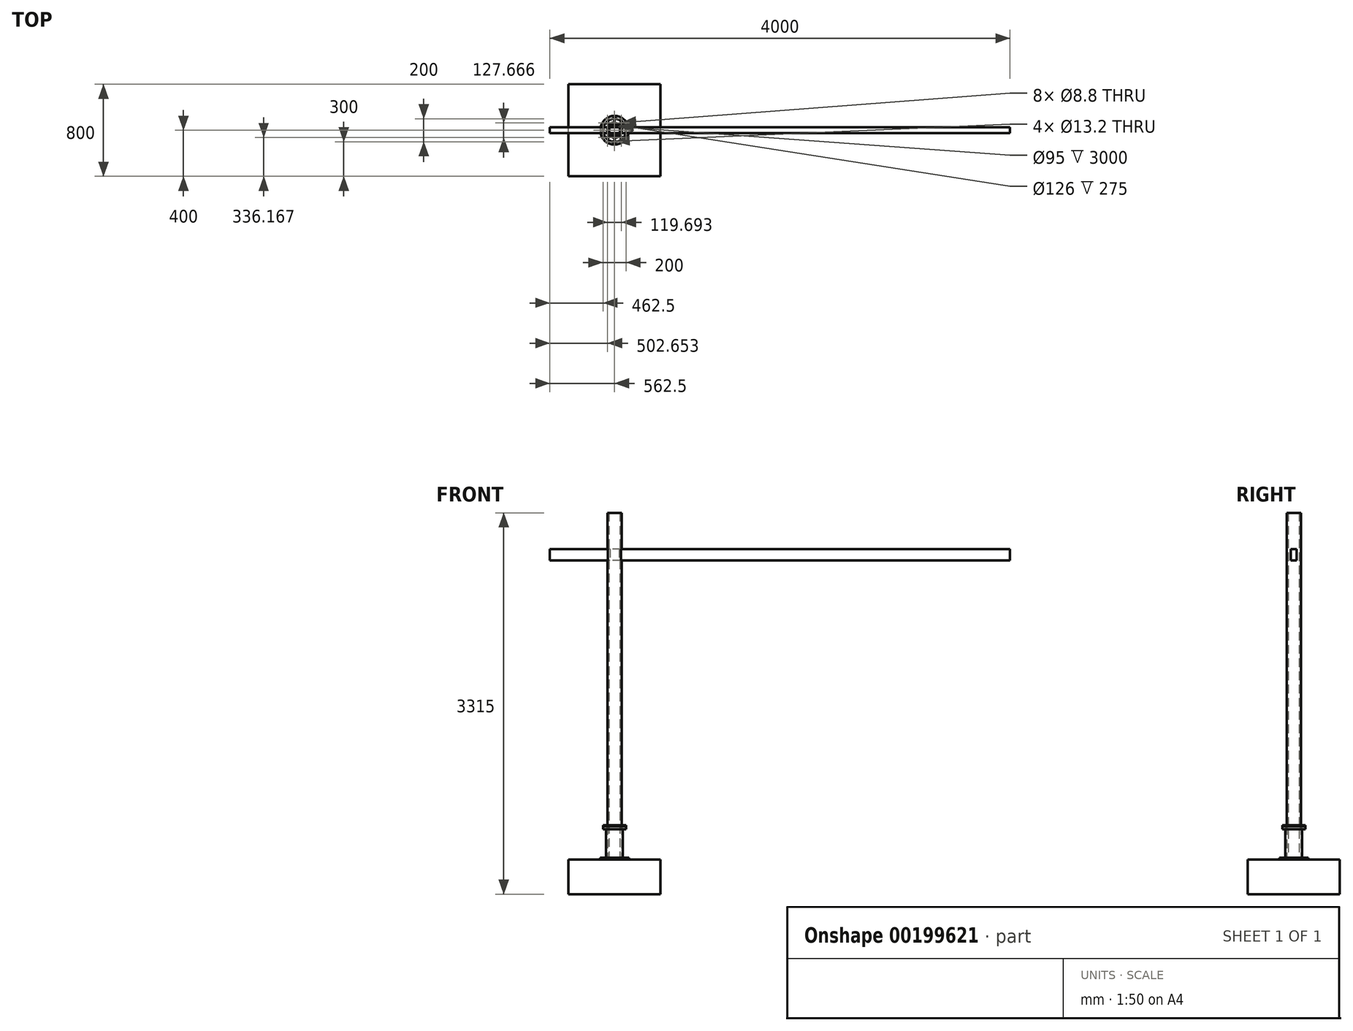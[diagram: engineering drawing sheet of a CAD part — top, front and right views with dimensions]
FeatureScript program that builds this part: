
annotation { "Feature Type Name" : "Feature", "Feature Type Description" : "" }
export const myFeature = defineFeature(function(context is Context, id is Id, definition is map)
    precondition{}
    {
        {
            var Q0;
            Q0=qCreatedBy(makeId("Top.planeOp"),FACE);
            var sketch = newSketch(context, id + "F0", { "sketchPlane" : qUnion([Q0])});
            skLineSegment(sketch, "E0.bottom", {"start": v(-400, -400) * mm, "end": v(400, -400) * mm});
            skLineSegment(sketch, "E0.top", {"start": v(-400, 400) * mm, "end": v(400, 400) * mm});
            skLineSegment(sketch, "E0.left", {"start": v(-400, -400) * mm, "end": v(-400, 400) * mm});
            skLineSegment(sketch, "E0.right", {"start": v(400, -400) * mm, "end": v(400, 400) * mm});
            skPoint(sketch, "E0.middle", {"position": v(0, 0) * mm});
            skSolve(sketch);
        }
        {
            var Q0;
            Q0 = qSketchRegion(id + "F0", true);
            extrude(context, id + "F1", {"entities" : qUnion([Q0]), "oppositeDirection" : true, "depth" : 300 * mm});
        }
        {
            var Q0;
            Q0=makeQuery(id+"F1.opExtrude","CAP_FACE",FACE,{"disambiguationData":[OSD([sQuery(id+"F0.wireOp",EDGE,"E0.bottom"),sQuery(id+"F0.wireOp",EDGE,"E0.top"),sQuery(id+"F0.wireOp",EDGE,"E0.left"),sQuery(id+"F0.wireOp",EDGE,"E0.right")])],"isStart":true});
            var sketch = newSketch(context, id + "F2", { "sketchPlane" : qUnion([Q0])});
            skCircle(sketch, "E1", {"center": v(0, 0) * mm, "radius": 125 * mm});
            skSolve(sketch);
        }
        {
            var Q0;
            Q0 = qSketchRegion(id + "F2", true);
            extrude(context, id + "F3", {"entities" : qUnion([Q0]), "depth" : 15 * mm});
        }
        {
            var Q0;
            Q0=makeQuery(id+"F3.opExtrude","CAP_FACE",FACE,{"disambiguationData":[OSD([sQuery(id+"F2.wireOp",EDGE,"E1")])],"isStart":false});
            var sketch = newSketch(context, id + "F4", { "sketchPlane" : qUnion([Q0])});
            skCircle(sketch, "E2", {"center": v(0, 0) * mm, "radius": 62.5 * mm});
            skCircle(sketch, "E3.0", {"center": v(0, 0) * mm, "radius": 47.5 * mm});
            skSolve(sketch);
        }
        {
            var Q0;
            Q0 = qSketchRegion(id + "F4", true);
            extrude(context, id + "F5", {"entities" : qUnion([Q0]), "depth" : 3000 * mm});
        }
        {
            var Q0;
            Q0=qCreatedBy(makeId("Right.planeOp"),FACE);
            cPlane(context, id + "F6", {"entities" : qUnion([Q0]), "cplaneType" : CPlaneType.OFFSET, "offset" : 62.5 * mm, "oppositeDirection" : true, "width" : 150 * mm, "height" : 150 * mm});
        }
        {
            var Q0;
            Q0=qCreatedBy(id+"F6.planeOp",FACE);
            var sketch = newSketch(context, id + "F7", { "sketchPlane" : qUnion([Q0])});
            skLineSegment(sketch, "E4.bottom", {"start": v(-25, 2700) * mm, "end": v(25, 2700) * mm});
            skLineSegment(sketch, "E4.top", {"start": v(-25, 2600) * mm, "end": v(25, 2600) * mm});
            skLineSegment(sketch, "E4.left", {"start": v(-25, 2700) * mm, "end": v(-25, 2600) * mm});
            skLineSegment(sketch, "E4.right", {"start": v(25, 2700) * mm, "end": v(25, 2600) * mm});
            skPoint(sketch, "E4.middle", {"position": v(0, 2650) * mm});
            skSolve(sketch);
        }
        {
            var Q0;
            Q0 = qSketchRegion(id + "F7", true);
            extrude(context, id + "F8", {"entities" : qUnion([Q0]), "operationType" : NewBodyOperationType.REMOVE, "endBound" : BoundingType.THROUGH_ALL, "depth" : 25 * mm});
        }
        {
            var Q0;
            Q0=qCreatedBy(id+"F6.planeOp",FACE);
            var sketch = newSketch(context, id + "F9", { "sketchPlane" : qUnion([Q0])});
            skLineSegment(sketch, "E5.bottom", {"start": v(25, 2600) * mm, "end": v(-25, 2600) * mm});
            skLineSegment(sketch, "E5.top", {"start": v(25, 2700) * mm, "end": v(-25, 2700) * mm});
            skLineSegment(sketch, "E5.left", {"start": v(25, 2600) * mm, "end": v(25, 2700) * mm});
            skLineSegment(sketch, "E5.right", {"start": v(-25, 2600) * mm, "end": v(-25, 2700) * mm});
            skSolve(sketch);
        }
        {
            var Q0;
            Q0 = qSketchRegion(id + "F9", true);
            extrude(context, id + "F10", {"entities" : qUnion([Q0]), "depth" : 3500 * mm, "hasSecondDirection" : true, "secondDirectionOppositeDirection" : true, "secondDirectionDepth" : 500 * mm});
        }
        {
            var Q0;
            Q0=makeQuery(id+"F3.opExtrude","CAP_FACE",FACE,{"disambiguationData":[OSD([sQuery(id+"F2.wireOp",EDGE,"E1")])],"isStart":false});
            var sketch = newSketch(context, id + "F11", { "sketchPlane" : qUnion([Q0])});
            skCircle(sketch, "E6", {"center": v(0, 0) * mm, "radius": 73 * mm});
            skCircle(sketch, "E7", {"center": v(0, 0) * mm, "radius": 63 * mm});
            skSolve(sketch);
        }
        {
            var Q0;
            Q0 = qSketchRegion(id + "F11", true);
            extrude(context, id + "F12", {"entities" : qUnion([Q0]), "operationType" : NewBodyOperationType.ADD, "depth" : 250 * mm});
        }
        {
            var Q0;
            Q0=makeQuery(id+"F12.opExtrude","CAP_FACE",FACE,{"disambiguationData":[OSD([sQuery(id+"F11.wireOp",EDGE,"E6"),sQuery(id+"F11.wireOp",EDGE,"E7")])],"isStart":false});
            var sketch = newSketch(context, id + "F13", { "sketchPlane" : qUnion([Q0])});
            skCircle(sketch, "E8", {"center": v(0, 0) * mm, "radius": 63 * mm});
            skCircle(sketch, "E9", {"center": v(0, 0) * mm, "radius": 100 * mm});
            skSolve(sketch);
        }
        {
            var Q0;
            Q0 = qSketchRegion(id + "F13", true);
            extrude(context, id + "F14", {"entities" : qUnion([Q0]), "operationType" : NewBodyOperationType.ADD, "depth" : 25 * mm});
        }
        {
            var Q0;
            Q0=makeQuery(id+"F14.opExtrude","CAP_FACE",FACE,{"disambiguationData":[OSD([sQuery(id+"F13.wireOp",EDGE,"E8"),sQuery(id+"F13.wireOp",EDGE,"E9")])],"isStart":false});
            var sketch = newSketch(context, id + "F15", { "sketchPlane" : qUnion([Q0])});
            skCircle(sketch, "E10", {"center": v(0, 0) * mm, "radius": 63 * mm});
            skCircle(sketch, "E11", {"center": v(0, 0) * mm, "radius": 58 * mm});
            skSolve(sketch);
        }
        {
            var Q0;
            Q0 = qSketchRegion(id + "F15", true);
            extrude(context, id + "F16", {"entities" : qUnion([Q0]), "operationType" : NewBodyOperationType.REMOVE, "depth" : 10 * mm});
        }
        {
            var Q0;
            Q0=makeQuery(id+"F14.opExtrude","CAP_FACE",FACE,{"disambiguationData":[OSD([sQuery(id+"F13.wireOp",EDGE,"E8"),sQuery(id+"F13.wireOp",EDGE,"E9")])],"isStart":false});
            var sketch = newSketch(context, id + "F17", { "sketchPlane" : qUnion([Q0])});
            skArc(sketch, "E12", {"start": v(0, -59) * mm, "mid": v(59, 0) * mm, "end": v(0, 59) * mm});
            skArc(sketch, "E13", {"start": v(0, -100) * mm, "mid": v(100, 0) * mm, "end": v(0, 100) * mm});
            skLineSegment(sketch, "E14", {"start": v(0, 100) * mm, "end": v(0, 59) * mm});
            skLineSegment(sketch, "E15.trimOffspring", {"start": v(0, -59) * mm, "end": v(0, -100) * mm});
            skSolve(sketch);
        }
        {
            var Q0;
            Q0 = qSketchRegion(id + "F17", true);
            extrude(context, id + "F18", {"entities" : qUnion([Q0]), "depth" : 8 * mm});
        }
        {
            var Q0;
            Q0=makeQuery(id+"F18.opExtrude","SWEPT_BODY",BODY,{"disambiguationData":[OSD([sQuery(id+"F17.wireOp",EDGE,"E12"),sQuery(id+"F17.wireOp",EDGE,"E13"),sQuery(id+"F17.wireOp",EDGE,"E14"),sQuery(id+"F17.wireOp",EDGE,"E15.trimOffspring")])]});
            var Q1;
            Q1=makeQuery(id+"F18.opExtrude","SWEPT_FACE",FACE,{"disambiguationData":[OSD([sQuery(id+"F17.wireOp",EDGE,"E15.trimOffspring")])]});
            mirror(context, id + "F19", {"entities" : qUnion([Q0]), "mirrorPlane" : qUnion([Q1])});
        }
        {
            var Q0;
            Q0=makeQuery(id+"F18.opExtrude","CAP_FACE",FACE,{"disambiguationData":[OSD([sQuery(id+"F17.wireOp",EDGE,"E12"),sQuery(id+"F17.wireOp",EDGE,"E13"),sQuery(id+"F17.wireOp",EDGE,"E14"),sQuery(id+"F17.wireOp",EDGE,"E15.trimOffspring")])],"isStart":false});
            var sketch = newSketch(context, id + "F20", { "sketchPlane" : qUnion([Q0])});
            skLineSegment(sketch, "E16", {"start": v(-59.85, -63.83) * mm, "end": v(59.85, 63.83) * mm, "construction": true});
            skCircle(sketch, "E17", {"center": v(0, 0) * mm, "radius": 87.5 * mm, "construction": true});
            skLineSegment(sketch, "E18.MirrorCS", {"start": v(59.85, -63.83) * mm, "end": v(-59.85, 63.83) * mm, "construction": true});
            skSolve(sketch);
        }
        {
            var Q0;
            Q0=sQuery(id+"F20.wireOp",VERTEX,"E18.MirrorCS.end");
            var Q1;
            Q1=sQuery(id+"F20.wireOp",VERTEX,"E16.end");
            var Q2;
            Q2=sQuery(id+"F20.wireOp",VERTEX,"E18.MirrorCS.start");
            var Q3;
            Q3=sQuery(id+"F20.wireOp",VERTEX,"E16.start");
            var Q4;
            Q4=makeQuery(id+"F3.opExtrude","SWEPT_BODY",BODY,{"disambiguationData":[OSD([sQuery(id+"F2.wireOp",EDGE,"E1")])]});
            var Q5;
            Q5=makeQuery(id+"F18.opExtrude","SWEPT_BODY",BODY,{"disambiguationData":[OSD([sQuery(id+"F17.wireOp",EDGE,"E12"),sQuery(id+"F17.wireOp",EDGE,"E13"),sQuery(id+"F17.wireOp",EDGE,"E14"),sQuery(id+"F17.wireOp",EDGE,"E15.trimOffspring")])]});
            var Q6;
            Q6=makeQuery(id+"F19.opPattern","COPY",BODY,{"derivedFrom":makeQuery(id+"F18.opExtrude","SWEPT_BODY",BODY,{"disambiguationData":[OSD([sQuery(id+"F17.wireOp",EDGE,"E12"),sQuery(id+"F17.wireOp",EDGE,"E13"),sQuery(id+"F17.wireOp",EDGE,"E14"),sQuery(id+"F17.wireOp",EDGE,"E15.trimOffspring")])]}),"instanceName":"1"});
            hole(context, id + "F21", {"style" : HoleStyle.C_SINK, "endStyle" : HoleEndStyle.BLIND, "standardTappedOrClearance" : lookupTablePath({ "standard" : "ISO", "fit" : "Normal", "size" : "M8", "type" : "Clearance" }), "standardBlindInLast" : lookupTablePath({ "fit" : "Standard", "standard" : "ISO", "size" : "M8", "type" : "Clearance" }), "holeDiameter" : 8.8 * mm, "cSinkDiameter" : 17.92 * mm, "cSinkAngle" : 90 * degree, "holeDepth" : 50 * mm, "locations" : qUnion([Q0, Q1, Q2, Q3]), "scope" : qUnion([Q4, Q5, Q6])});
        }
        {
            var Q0;
            {var subQ0=sQuery(id+"F2.wireOp",EDGE,"E1");Q0=makeQuery(id+"F12.boolean.opBoolean","SPLIT",FACE,{"disambiguationData":[TD([makeQuery(id+"F3.opExtrude","SWEPT_FACE",FACE,{"disambiguationData":[OSD([subQ0])]})])],"derivedFrom":makeQuery(id+"F3.opExtrude","CAP_FACE",FACE,{"disambiguationData":[OSD([subQ0])],"isStart":false})});}
            var sketch = newSketch(context, id + "F22", { "sketchPlane" : qUnion([Q0])});
            skCircle(sketch, "E19", {"center": v(0, 0) * mm, "radius": 100 * mm, "construction": true});
            skLineSegment(sketch, "E20", {"start": v(-100, 0) * mm, "end": v(100, 0) * mm, "construction": true});
            skLineSegment(sketch, "E21", {"start": v(0, 100) * mm, "end": v(0, -100) * mm, "construction": true});
            skSolve(sketch);
        }
        {
            var Q0;
            Q0=sQuery(id+"F22.wireOp",VERTEX,"E21.start");
            var Q1;
            Q1=sQuery(id+"F22.wireOp",VERTEX,"E21.end");
            var Q2;
            Q2=sQuery(id+"F22.wireOp",VERTEX,"E20.end");
            var Q3;
            Q3=sQuery(id+"F22.wireOp",VERTEX,"E20.start");
            var Q4;
            Q4=makeQuery(id+"F3.opExtrude","SWEPT_BODY",BODY,{"disambiguationData":[OSD([sQuery(id+"F2.wireOp",EDGE,"E1")])]});
            hole(context, id + "F23", {"style" : HoleStyle.C_SINK, "endStyle" : HoleEndStyle.BLIND, "standardTappedOrClearance" : lookupTablePath({ "standard" : "ISO", "fit" : "Normal", "size" : "M12", "type" : "Clearance" }), "standardBlindInLast" : lookupTablePath({ "fit" : "Standard", "standard" : "ISO", "size" : "M12", "type" : "Clearance" }), "holeDiameter" : 13.2 * mm, "cSinkDiameter" : 26.88 * mm, "cSinkAngle" : 90 * degree, "holeDepth" : 50 * mm, "locations" : qUnion([Q0, Q1, Q2, Q3]), "scope" : qUnion([Q4])});
        }
        {
            var Q0;
            Q0=qCreatedBy(makeId("Front.planeOp"),FACE);
            var sketch = newSketch(context, id + "F24", { "sketchPlane" : qUnion([Q0])});
            skLineSegment(sketch, "E22", {"start": v(0, 2071.46) * mm, "end": v(1426.94, 2895.3) * mm, "construction": true});
            skLineSegment(sketch, "E23", {"start": v(1091.8, 2701.81) * mm, "end": v(1091.8, 2362.52) * mm, "construction": true});
            skLineSegment(sketch, "E24", {"start": v(915.63, 2600.1) * mm, "end": v(915.63, 2350.37) * mm, "construction": true});
            skLineSegment(sketch, "E25", {"start": v(1091.8, 2701.81) * mm, "end": v(915.63, 2600.1) * mm, "construction": true});
            skLineSegment(sketch, "E26", {"start": v(1003.71, 2650.96) * mm, "end": v(1148.36, 2400.42) * mm, "construction": true});
            skSolve(sketch);
        }
        {
            var Q0;
            Q0=sQuery(id+"F24.wireOp",EDGE,"E26");
            var Q1;
            Q1=sQuery(id+"F24.wireOp",EDGE,"E22");
            cPlane(context, id + "F25", {"entities" : qUnion([Q0, Q1]), "cplaneType" : CPlaneType.LINE_ANGLE, "offset" : 25 * mm, "angle" : 90 * degree, "width" : 150 * mm, "height" : 150 * mm});
        }
    });
